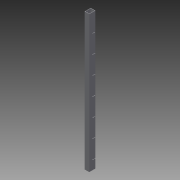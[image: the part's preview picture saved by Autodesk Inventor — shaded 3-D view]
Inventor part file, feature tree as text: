
AUTODESK INVENTOR PART (.ipt)
format: ipt  version: 2013 (Build 170138000, 138)  size: 124,928 bytes
history: native  units: in
note: dims shown in document units (in); Inventor stores cm internally (conversion verified against a paired STEP export)
features: other x4, extrude x1, sketch x1
ambient origin geometry x8: Origin, YZ Plane, XZ Plane, XY Plane, X Axis, Y Axis, Z Axis, Center Point
bodies: Solid1 (feature_tree)
feature tree (6):
  other  "Table"
  other  "squareTube1.5x2.ipt"
  extrude  "Extrusion1"  TaperAngle=0.0deg  [1 undecoded]
  other  "Solid1::squareTube1.5x2.ipt"
  other  "TaggingFeature1"
  sketch  "Sketch1"  dims[d0=1.5in d1=2.0in d2=0.125in d4=0.0in d3=0.25in d5=0.125in d6=6.0in d7=2.7559in d9=6.0in d10=0.3937in d12=1.0in d14=1.0in d15=0.0in]
note: 1 required parameter value undecoded (feature->parameter linkage not recoverable at this tier; creation-order binding heuristic only, values carry confidence <= 0.55)
